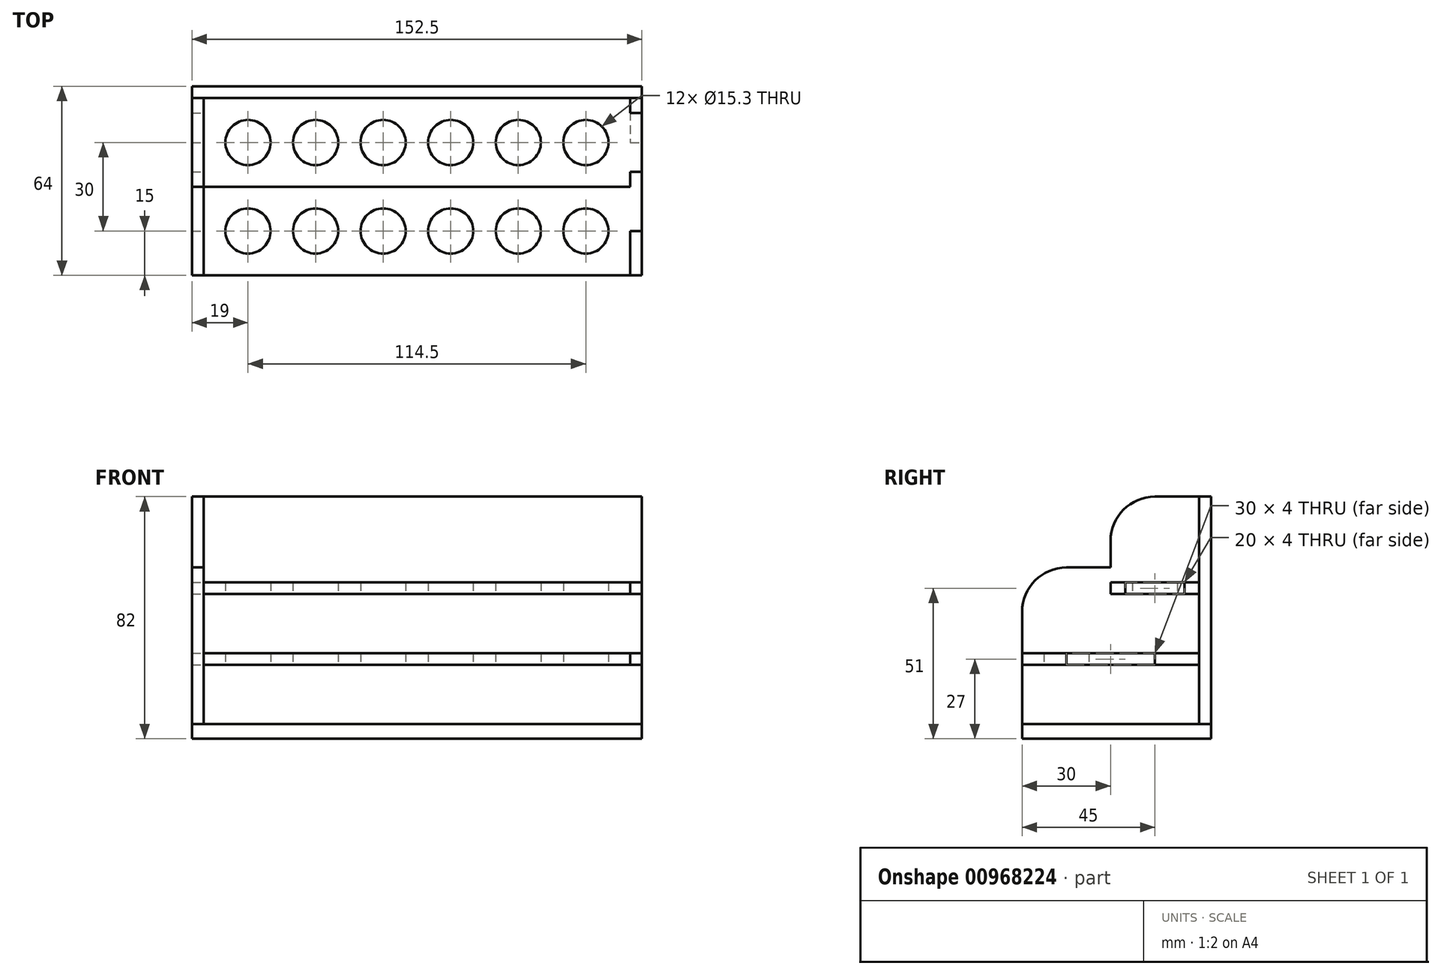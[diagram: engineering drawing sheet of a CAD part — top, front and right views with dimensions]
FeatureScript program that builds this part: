
annotation { "Feature Type Name" : "Feature", "Feature Type Description" : "" }
export const myFeature = defineFeature(function(context is Context, id is Id, definition is map)
    precondition{}
    {
        {
            var Q0;
            Q0=qCreatedBy(makeId("Top.planeOp"),FACE);
            var sketch = newSketch(context, id + "F0", { "sketchPlane" : qUnion([Q0])});
            skLineSegment(sketch, "E0.bottom", {"start": v(-72.25, 60) * mm, "end": v(72.25, 60) * mm});
            skLineSegment(sketch, "E0.top", {"start": v(-72.25, 0) * mm, "end": v(72.25, 0) * mm});
            skLineSegment(sketch, "E0.left", {"start": v(-72.25, 60) * mm, "end": v(-72.25, 45) * mm});
            skLineSegment(sketch, "E0.right", {"start": v(72.25, 60) * mm, "end": v(72.25, 45) * mm});
            skLineSegment(sketch, "E1", {"start": v(72.25, 15) * mm, "end": v(72.25, 0) * mm});
            skCircle(sketch, "E2", {"center": v(-57.25, 15) * mm, "radius": 7.65 * mm});
            skCircle(sketch, "E3.1.0.0", {"center": v(-34.35, 15) * mm, "radius": 7.65 * mm});
            skCircle(sketch, "E3.2.0.0", {"center": v(-11.45, 15) * mm, "radius": 7.65 * mm});
            skCircle(sketch, "E3.3.0.0", {"center": v(11.45, 15) * mm, "radius": 7.65 * mm});
            skCircle(sketch, "E3.4.0.0", {"center": v(34.35, 15) * mm, "radius": 7.65 * mm});
            skCircle(sketch, "E3.5.0.0", {"center": v(57.25, 15) * mm, "radius": 7.65 * mm});
            skLineSegment(sketch, "E3.direction1", {"start": v(-57.25, 15) * mm, "end": v(-34.35, 15) * mm, "construction": true});
            skLineSegment(sketch, "E4.bottom", {"start": v(-72.25, 45) * mm, "end": v(-76.25, 45) * mm});
            skLineSegment(sketch, "E4.top", {"start": v(-72.25, 15) * mm, "end": v(-76.25, 15) * mm});
            skLineSegment(sketch, "E4.right", {"start": v(-76.25, 45) * mm, "end": v(-76.25, 15) * mm});
            skLineSegment(sketch, "E5.bottom", {"start": v(72.25, 45) * mm, "end": v(76.25, 45) * mm});
            skLineSegment(sketch, "E5.top", {"start": v(72.25, 15) * mm, "end": v(76.25, 15) * mm});
            skLineSegment(sketch, "E5.right", {"start": v(76.25, 45) * mm, "end": v(76.25, 15) * mm});
            skLineSegment(sketch, "E6.trimOffspring", {"start": v(-72.25, 15) * mm, "end": v(-72.25, 0) * mm});
            skSolve(sketch);
        }
        {
            var Q0;
            {var subQ0=sQuery(id+"F0.wireOp",EDGE,"E0.bottom");Q0=makeQuery(id+"F0.imprint","IMPRINT",FACE,{"disambiguationData":[TD([[makeQuery(id+"F0.imprint","IMPRINT",EDGE,{"derivedFrom":subQ0}),-1.0]])]});}
            var Q1;
            Q1=makeQuery(id+"F0.imprint","IMPRINT",FACE,{"disambiguationData":[TD([[makeQuery(id+"F0.imprint","IMPRINT",EDGE,{"derivedFrom":sQuery(id+"F0.wireOp",EDGE,"E4.bottom")}),1.0]])]});
            var Q2;
            Q2=makeQuery(id+"F0.imprint","IMPRINT",FACE,{"disambiguationData":[TD([[makeQuery(id+"F0.imprint","IMPRINT",EDGE,{"derivedFrom":sQuery(id+"F0.wireOp",EDGE,"E5.bottom")}),-1.0]])]});
            extrude(context, id + "F1", {"entities" : qUnion([Q0, Q1, Q2]), "depth" : 4 * mm, "offsetDistance" : 25 * mm});
        }
        {
            var Q0;
            {var subQ0=sQuery(id+"F0.wireOp",EDGE,"E0.left");Q0=makeQuery(id+"F1.opExtrude","SWEPT_FACE",FACE,{"disambiguationData":[OSD([subQ0]),TDD([makeQuery(id+"F0.imprint","IMPRINT",EDGE,{"disambiguationData":[TD([[makeQuery(id+"F0.imprint","INTERSECT",VERTEX,{"derivedFrom":[sQuery(id+"F0.wireOp",EDGE,"E0.bottom"),subQ0]}),-1.0]])],"derivedFrom":subQ0})])]});}
            var sketch = newSketch(context, id + "F2", { "sketchPlane" : qUnion([Q0])});
            skLineSegment(sketch, "E7.bottom", {"start": v(-60, -20) * mm, "end": v(0, -20) * mm});
            skLineSegment(sketch, "E7.top", {"start": v(-30, 33) * mm, "end": v(-15, 33) * mm});
            skLineSegment(sketch, "E7.left", {"start": v(-60, -20) * mm, "end": v(-60, 33) * mm});
            skLineSegment(sketch, "E7.right", {"start": v(0, -20) * mm, "end": v(0, 18) * mm});
            skPoint(sketch, "E8.0", {"position": v(-15, 0) * mm});
            skPoint(sketch, "E9.0", {"position": v(-45, 4) * mm});
            skLineSegment(sketch, "E10.bottom", {"start": v(-45, 4) * mm, "end": v(-15, 4) * mm});
            skLineSegment(sketch, "E10.top", {"start": v(-45, 0) * mm, "end": v(-15, 0) * mm});
            skLineSegment(sketch, "E10.left", {"start": v(-45, 4) * mm, "end": v(-45, 0) * mm});
            skLineSegment(sketch, "E10.right", {"start": v(-15, 4) * mm, "end": v(-15, 0) * mm});
            skPoint(sketch, "E11.visualSharp", {"position": v(0, 33) * mm});
            skArc(sketch, "E11.filletArc", {"start": v(0, 18) * mm, "mid": v(-4.4, 28.6) * mm, "end": v(-15, 33) * mm});
            skPoint(sketch, "E12.firstSnap0", {"position": v(-30, 4) * mm});
            skLineSegment(sketch, "E12.top", {"start": v(-45, 57) * mm, "end": v(-60, 57) * mm});
            skLineSegment(sketch, "E12.left", {"start": v(-30, 33) * mm, "end": v(-30, 42) * mm});
            skLineSegment(sketch, "E12.right", {"start": v(-60, 33) * mm, "end": v(-60, 57) * mm});
            skPoint(sketch, "E13.visualSharp", {"position": v(-30, 57) * mm});
            skArc(sketch, "E13.filletArc", {"start": v(-30, 42) * mm, "mid": v(-34.4, 52.6) * mm, "end": v(-45, 57) * mm});
            skLineSegment(sketch, "E14.bottom", {"start": v(-55, 28) * mm, "end": v(-35, 28) * mm});
            skLineSegment(sketch, "E14.top", {"start": v(-55, 24) * mm, "end": v(-35, 24) * mm});
            skLineSegment(sketch, "E14.left", {"start": v(-55, 28) * mm, "end": v(-55, 24) * mm});
            skLineSegment(sketch, "E14.right", {"start": v(-35, 28) * mm, "end": v(-35, 24) * mm});
            skSolve(sketch);
        }
        {
            var Q0;
            Q0 = qSketchRegion(id + "F2", true);
            extrude(context, id + "F3", {"entities" : qUnion([Q0]), "depth" : 4 * mm, "offsetDistance" : 25 * mm});
        }
        {
            var Q0;
            Q0=makeQuery(id+"F1.opExtrude","CAP_FACE",FACE,{"disambiguationData":[OSD([sQuery(id+"F0.wireOp",EDGE,"E0.bottom"),sQuery(id+"F0.wireOp",EDGE,"E0.top"),sQuery(id+"F0.wireOp",EDGE,"E0.left"),sQuery(id+"F0.wireOp",EDGE,"E0.right"),sQuery(id+"F0.wireOp",EDGE,"E1"),sQuery(id+"F0.wireOp",EDGE,"E2"),sQuery(id+"F0.wireOp",EDGE,"E3.1.0.0"),sQuery(id+"F0.wireOp",EDGE,"E3.2.0.0"),sQuery(id+"F0.wireOp",EDGE,"E3.3.0.0"),sQuery(id+"F0.wireOp",EDGE,"E3.4.0.0"),sQuery(id+"F0.wireOp",EDGE,"E3.5.0.0"),sQuery(id+"F0.wireOp",EDGE,"E4.bottom"),sQuery(id+"F0.wireOp",EDGE,"E4.top"),sQuery(id+"F0.wireOp",EDGE,"E4.right"),sQuery(id+"F0.wireOp",EDGE,"E5.bottom"),sQuery(id+"F0.wireOp",EDGE,"E5.top"),sQuery(id+"F0.wireOp",EDGE,"E5.right")])],"isStart":false});
            cPlane(context, id + "F4", {"entities" : qUnion([Q0]), "cplaneType" : CPlaneType.OFFSET, "offset" : 20 * mm, "width" : 150 * mm, "height" : 150 * mm});
        }
        {
            var Q0;
            Q0=qCreatedBy(id+"F4.planeOp",FACE);
            var sketch = newSketch(context, id + "F5", { "sketchPlane" : qUnion([Q0])});
            skPoint(sketch, "E15.0", {"position": v(-72.25, 60) * mm});
            skPoint(sketch, "E16.0", {"position": v(72.25, 60) * mm});
            skLineSegment(sketch, "E17.bottom", {"start": v(-72.25, 60) * mm, "end": v(72.25, 60) * mm});
            skLineSegment(sketch, "E17.top", {"start": v(-72.25, 30) * mm, "end": v(72.25, 30) * mm});
            skLineSegment(sketch, "E17.left", {"start": v(-72.25, 60) * mm, "end": v(-72.25, 55) * mm});
            skLineSegment(sketch, "E17.right", {"start": v(72.25, 60) * mm, "end": v(72.25, 55) * mm});
            skPoint(sketch, "E18.0", {"position": v(-76.25, 35) * mm});
            skPoint(sketch, "E19.0", {"position": v(-76.25, 55) * mm});
            skLineSegment(sketch, "E20.bottom", {"start": v(-76.25, 55) * mm, "end": v(-72.25, 55) * mm});
            skLineSegment(sketch, "E20.top", {"start": v(-76.25, 35) * mm, "end": v(-72.25, 35) * mm});
            skLineSegment(sketch, "E20.left", {"start": v(-76.25, 55) * mm, "end": v(-76.25, 35) * mm});
            skLineSegment(sketch, "E21.trimOffspring", {"start": v(-72.25, 35) * mm, "end": v(-72.25, 30) * mm});
            skLineSegment(sketch, "E22.bottom", {"start": v(72.25, 55) * mm, "end": v(76.25, 55) * mm});
            skLineSegment(sketch, "E22.top", {"start": v(72.25, 35) * mm, "end": v(76.25, 35) * mm});
            skLineSegment(sketch, "E22.right", {"start": v(76.25, 55) * mm, "end": v(76.25, 35) * mm});
            skLineSegment(sketch, "E23.trimOffspring", {"start": v(72.25, 35) * mm, "end": v(72.25, 30) * mm});
            skCircle(sketch, "E24", {"center": v(-57.25, 45) * mm, "radius": 7.65 * mm});
            skPoint(sketch, "E24.centerSnap0", {"position": v(-76.25, 45) * mm});
            skCircle(sketch, "E25.1.0.0", {"center": v(-34.35, 45) * mm, "radius": 7.65 * mm});
            skCircle(sketch, "E25.2.0.0", {"center": v(-11.45, 45) * mm, "radius": 7.65 * mm});
            skCircle(sketch, "E25.3.0.0", {"center": v(11.45, 45) * mm, "radius": 7.65 * mm});
            skCircle(sketch, "E25.4.0.0", {"center": v(34.35, 45) * mm, "radius": 7.65 * mm});
            skCircle(sketch, "E25.5.0.0", {"center": v(57.25, 45) * mm, "radius": 7.65 * mm});
            skLineSegment(sketch, "E25.direction1", {"start": v(-57.25, 45) * mm, "end": v(-34.35, 45) * mm, "construction": true});
            skSolve(sketch);
        }
        {
            var Q0;
            Q0=makeQuery(id+"F5.imprint","IMPRINT",FACE,{"disambiguationData":[TD([[makeQuery(id+"F5.imprint","IMPRINT",EDGE,{"derivedFrom":sQuery(id+"F5.wireOp",EDGE,"E17.bottom")}),-1.0]])]});
            extrude(context, id + "F6", {"entities" : qUnion([Q0]), "depth" : 4 * mm, "offsetDistance" : 25 * mm});
        }
        {
            var Q0;
            Q0=makeQuery(id+"F3.opExtrude","SWEPT_FACE",FACE,{"disambiguationData":[OSD([sQuery(id+"F2.wireOp",EDGE,"E7.left"),sQuery(id+"F2.wireOp",EDGE,"E12.right")])]});
            var sketch = newSketch(context, id + "F7", { "sketchPlane" : qUnion([Q0])});
            skPoint(sketch, "E26.0", {"position": v(76.25, 57) * mm});
            skPoint(sketch, "E27.0", {"position": v(76.25, -20) * mm});
            skPoint(sketch, "E28.0", {"position": v(-76.25, 0) * mm});
            skLineSegment(sketch, "E29.bottom", {"start": v(76.25, 57) * mm, "end": v(-76.25, 57) * mm});
            skLineSegment(sketch, "E29.top", {"start": v(76.25, -20) * mm, "end": v(-76.25, -20) * mm});
            skLineSegment(sketch, "E29.left", {"start": v(76.25, 57) * mm, "end": v(76.25, -20) * mm});
            skLineSegment(sketch, "E29.right", {"start": v(-76.25, 57) * mm, "end": v(-76.25, -20) * mm});
            skSolve(sketch);
        }
        {
            var Q0;
            Q0 = qSketchRegion(id + "F7", true);
            extrude(context, id + "F8", {"entities" : qUnion([Q0]), "depth" : 4 * mm, "offsetDistance" : 25 * mm});
        }
        {
            var Q0;
            Q0=makeQuery(id+"F8.opExtrude","SWEPT_FACE",FACE,{"disambiguationData":[OSD([sQuery(id+"F7.wireOp",EDGE,"E29.top")])]});
            var sketch = newSketch(context, id + "F9", { "sketchPlane" : qUnion([Q0])});
            skPoint(sketch, "E30.0", {"position": v(-76.25, -64) * mm});
            skPoint(sketch, "E31.0", {"position": v(-76.25, 0) * mm});
            skPoint(sketch, "E32.0", {"position": v(76.25, -15) * mm});
            skLineSegment(sketch, "E33.bottom", {"start": v(-76.25, -64) * mm, "end": v(76.25, -64) * mm});
            skLineSegment(sketch, "E33.top", {"start": v(-76.25, 0) * mm, "end": v(76.25, 0) * mm});
            skLineSegment(sketch, "E33.left", {"start": v(-76.25, -64) * mm, "end": v(-76.25, 0) * mm});
            skLineSegment(sketch, "E33.right", {"start": v(76.25, -64) * mm, "end": v(76.25, 0) * mm});
            skSolve(sketch);
        }
        {
            var Q0;
            Q0 = qSketchRegion(id + "F9", true);
            extrude(context, id + "F10", {"entities" : qUnion([Q0]), "depth" : 5 * mm, "offsetDistance" : 25 * mm});
        }
    });
